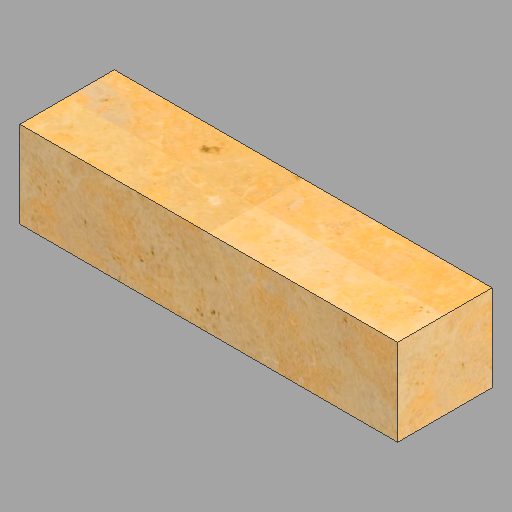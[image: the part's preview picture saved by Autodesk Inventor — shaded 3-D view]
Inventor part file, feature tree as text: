
AUTODESK INVENTOR PART (.ipt)
format: ipt  version: 2023 (Build 270158030, 158C)  size: 288,256 bytes
history: native  units: in
note: dims shown in document units (in); Inventor stores cm internally (conversion verified against a paired STEP export)
features: extrude x1, sketch x1
ambient origin geometry x8: Origin, YZ Plane, XZ Plane, XY Plane, X Axis, Y Axis, Z Axis, Center Point
bodies: Solid1 (feature_tree)
feature tree (2):
  extrude  "Extrusion1"  Depth=3.0in
  sketch  "Sketch1"  dims[d0=12.0in d1=3.0in d2=2.75in d3=0.0in]
